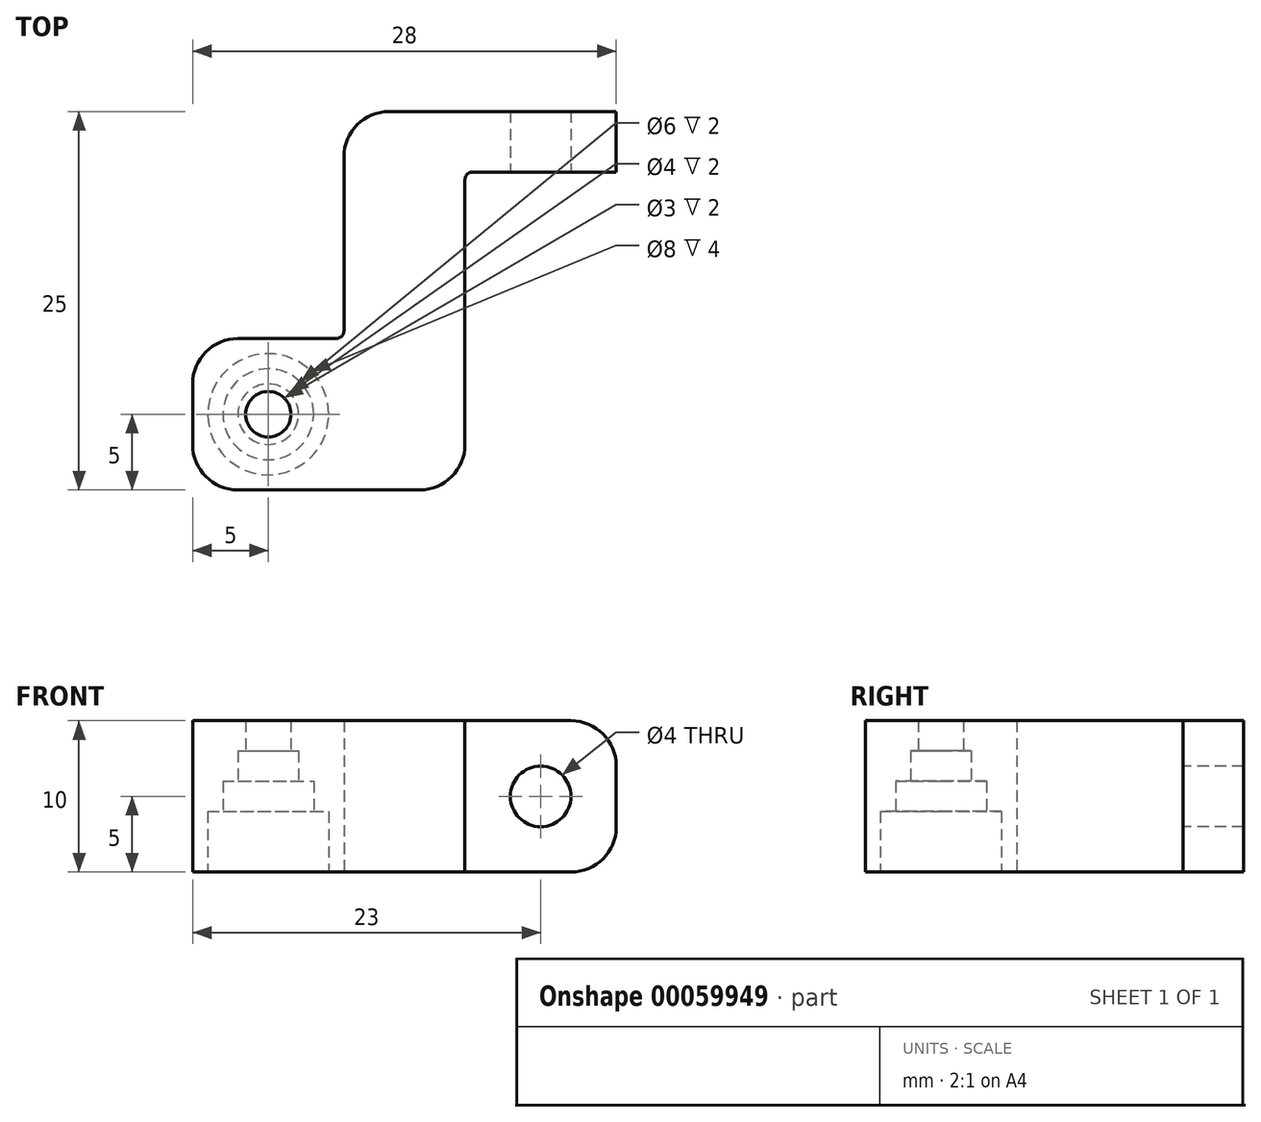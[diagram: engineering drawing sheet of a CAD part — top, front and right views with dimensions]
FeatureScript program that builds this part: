
annotation { "Feature Type Name" : "Feature", "Feature Type Description" : "" }
export const myFeature = defineFeature(function(context is Context, id is Id, definition is map)
    precondition{}
    {
        {
            var Q0;
            Q0=qCreatedBy(makeId("Top.planeOp"),FACE);
            var sketch = newSketch(context, id + "F0", { "sketchPlane" : qUnion([Q0])});
            skLineSegment(sketch, "E0.rect.bottom", {"start": v(4, 12.5) * mm, "end": v(-4, 12.5) * mm});
            skLineSegment(sketch, "E0.rect.top", {"start": v(4, -12.5) * mm, "end": v(-4, -12.5) * mm});
            skLineSegment(sketch, "E0.rect.left", {"start": v(4, 8.5) * mm, "end": v(4, -12.5) * mm});
            skLineSegment(sketch, "E0.rect.right", {"start": v(-4, 12.5) * mm, "end": v(-4, -2.5) * mm});
            skPoint(sketch, "E0.rect.middle", {"position": v(0, 0) * mm});
            skLineSegment(sketch, "E1.bottom", {"start": v(4, 12.5) * mm, "end": v(14, 12.5) * mm});
            skLineSegment(sketch, "E1.top", {"start": v(4, 8.5) * mm, "end": v(14, 8.5) * mm});
            skLineSegment(sketch, "E1.right", {"start": v(14, 12.5) * mm, "end": v(14, 8.5) * mm});
            skLineSegment(sketch, "E2.bottom", {"start": v(-4, -12.5) * mm, "end": v(-14, -12.5) * mm});
            skLineSegment(sketch, "E2.top", {"start": v(-4, -2.5) * mm, "end": v(-14, -2.5) * mm});
            skLineSegment(sketch, "E2.right", {"start": v(-14, -12.5) * mm, "end": v(-14, -2.5) * mm});
            skLineSegment(sketch, "E3", {"start": v(4, 8.5) * mm, "end": v(4, 12.5) * mm, "construction": true});
            skLineSegment(sketch, "E4", {"start": v(-4, -12.5) * mm, "end": v(-4, -2.5) * mm, "construction": true});
            skLineSegment(sketch, "E5", {"start": v(-4, -12.5) * mm, "end": v(-14, -2.5) * mm, "construction": true});
            skSolve(sketch);
        }
        {
            var Q0;
            Q0 = qSketchRegion(id + "F0", true);
            extrude(context, id + "F1", {"entities" : qUnion([Q0]), "depth" : 10 * mm});
        }
        {
            var Q0;
            Q0=makeQuery(id+"F1.opExtrude","SWEPT_EDGE",EDGE,{"disambiguationData":[OSD([sQuery(id+"F0.wireOp",EDGE,"E0.rect.bottom"),sQuery(id+"F0.wireOp",EDGE,"E0.rect.right")])]});
            var Q1;
            Q1=makeQuery(id+"F1.opExtrude","SWEPT_EDGE",EDGE,{"disambiguationData":[OSD([sQuery(id+"F0.wireOp",EDGE,"E0.rect.top"),sQuery(id+"F0.wireOp",EDGE,"E0.rect.left")])]});
            fillet(context, id + "F2", {"entities" : qUnion([Q0, Q1]), "radius" : 3 * mm, "tangentPropagation" : true, "allowEdgeOverflow" : false});
        }
        {
            var Q0;
            Q0=makeQuery(id+"F1.opExtrude","CAP_FACE",FACE,{"disambiguationData":[OSD([sQuery(id+"F0.wireOp",EDGE,"E0.rect.bottom"),sQuery(id+"F0.wireOp",EDGE,"E0.rect.top"),sQuery(id+"F0.wireOp",EDGE,"E0.rect.left"),sQuery(id+"F0.wireOp",EDGE,"E0.rect.right"),sQuery(id+"F0.wireOp",EDGE,"E1.bottom"),sQuery(id+"F0.wireOp",EDGE,"E1.top"),sQuery(id+"F0.wireOp",EDGE,"E1.right"),sQuery(id+"F0.wireOp",EDGE,"E2.bottom"),sQuery(id+"F0.wireOp",EDGE,"E2.top"),sQuery(id+"F0.wireOp",EDGE,"E2.right")])],"isStart":true});
            var sketch = newSketch(context, id + "F3", { "sketchPlane" : qUnion([Q0])});
            skLineSegment(sketch, "E6", {"start": v(-4, 2.5) * mm, "end": v(-14, 12.5) * mm, "construction": true});
            skCircle(sketch, "E7", {"center": v(-9, 7.5) * mm, "radius": 1.5 * mm});
            skSolve(sketch);
        }
        {
            var Q0;
            Q0 = qSketchRegion(id + "F3", true);
            extrude(context, id + "F4", {"entities" : qUnion([Q0]), "operationType" : NewBodyOperationType.REMOVE, "endBound" : BoundingType.THROUGH_ALL, "oppositeDirection" : true, "depth" : 25 * mm});
        }
        {
            var Q0;
            Q0=makeQuery(id+"F1.opExtrude","CAP_FACE",FACE,{"disambiguationData":[OSD([sQuery(id+"F0.wireOp",EDGE,"E0.rect.bottom"),sQuery(id+"F0.wireOp",EDGE,"E0.rect.top"),sQuery(id+"F0.wireOp",EDGE,"E0.rect.left"),sQuery(id+"F0.wireOp",EDGE,"E0.rect.right"),sQuery(id+"F0.wireOp",EDGE,"E1.bottom"),sQuery(id+"F0.wireOp",EDGE,"E1.top"),sQuery(id+"F0.wireOp",EDGE,"E1.right"),sQuery(id+"F0.wireOp",EDGE,"E2.bottom"),sQuery(id+"F0.wireOp",EDGE,"E2.top"),sQuery(id+"F0.wireOp",EDGE,"E2.right")])],"isStart":true});
            var sketch = newSketch(context, id + "F5", { "sketchPlane" : qUnion([Q0])});
            skCircle(sketch, "E8", {"center": v(-9, 7.5) * mm, "radius": 2 * mm});
            skSolve(sketch);
        }
        {
            var Q0;
            Q0 = qSketchRegion(id + "F5", true);
            extrude(context, id + "F6", {"entities" : qUnion([Q0]), "operationType" : NewBodyOperationType.REMOVE, "oppositeDirection" : true, "depth" : 8 * mm});
        }
        {
            var Q0;
            Q0=makeQuery(id+"F1.opExtrude","CAP_FACE",FACE,{"disambiguationData":[OSD([sQuery(id+"F0.wireOp",EDGE,"E0.rect.bottom"),sQuery(id+"F0.wireOp",EDGE,"E0.rect.top"),sQuery(id+"F0.wireOp",EDGE,"E0.rect.left"),sQuery(id+"F0.wireOp",EDGE,"E0.rect.right"),sQuery(id+"F0.wireOp",EDGE,"E1.bottom"),sQuery(id+"F0.wireOp",EDGE,"E1.top"),sQuery(id+"F0.wireOp",EDGE,"E1.right"),sQuery(id+"F0.wireOp",EDGE,"E2.bottom"),sQuery(id+"F0.wireOp",EDGE,"E2.top"),sQuery(id+"F0.wireOp",EDGE,"E2.right")])],"isStart":true});
            var sketch = newSketch(context, id + "F7", { "sketchPlane" : qUnion([Q0])});
            skCircle(sketch, "E9", {"center": v(-9, 7.5) * mm, "radius": 3 * mm});
            skSolve(sketch);
        }
        {
            var Q0;
            Q0 = qSketchRegion(id + "F7", true);
            extrude(context, id + "F8", {"entities" : qUnion([Q0]), "operationType" : NewBodyOperationType.REMOVE, "oppositeDirection" : true, "depth" : 6 * mm});
        }
        {
            var Q0;
            Q0=makeQuery(id+"F1.opExtrude","CAP_FACE",FACE,{"disambiguationData":[OSD([sQuery(id+"F0.wireOp",EDGE,"E0.rect.bottom"),sQuery(id+"F0.wireOp",EDGE,"E0.rect.top"),sQuery(id+"F0.wireOp",EDGE,"E0.rect.left"),sQuery(id+"F0.wireOp",EDGE,"E0.rect.right"),sQuery(id+"F0.wireOp",EDGE,"E1.bottom"),sQuery(id+"F0.wireOp",EDGE,"E1.top"),sQuery(id+"F0.wireOp",EDGE,"E1.right"),sQuery(id+"F0.wireOp",EDGE,"E2.bottom"),sQuery(id+"F0.wireOp",EDGE,"E2.top"),sQuery(id+"F0.wireOp",EDGE,"E2.right")])],"isStart":true});
            var sketch = newSketch(context, id + "F9", { "sketchPlane" : qUnion([Q0])});
            skCircle(sketch, "E10", {"center": v(-9, 7.5) * mm, "radius": 4 * mm});
            skSolve(sketch);
        }
        {
            var Q0;
            Q0 = qSketchRegion(id + "F9", true);
            extrude(context, id + "F10", {"entities" : qUnion([Q0]), "operationType" : NewBodyOperationType.REMOVE, "oppositeDirection" : true, "depth" : 4 * mm});
        }
        {
            var Q0;
            Q0=makeQuery(id+"F1.opExtrude","SWEPT_EDGE",EDGE,{"disambiguationData":[OSD([sQuery(id+"F0.wireOp",EDGE,"E2.top"),sQuery(id+"F0.wireOp",EDGE,"E2.right")])]});
            var Q1;
            Q1=makeQuery(id+"F1.opExtrude","SWEPT_EDGE",EDGE,{"disambiguationData":[OSD([sQuery(id+"F0.wireOp",EDGE,"E2.bottom"),sQuery(id+"F0.wireOp",EDGE,"E2.right")])]});
            fillet(context, id + "F11", {"entities" : qUnion([Q0, Q1]), "radius" : 3 * mm, "tangentPropagation" : true, "allowEdgeOverflow" : false});
        }
        {
            var Q0;
            Q0=makeQuery(id+"F1.opExtrude","SWEPT_FACE",FACE,{"disambiguationData":[OSD([sQuery(id+"F0.wireOp",EDGE,"E1.top")])]});
            var sketch = newSketch(context, id + "F12", { "sketchPlane" : qUnion([Q0])});
            skLineSegment(sketch, "E11", {"start": v(4, 0) * mm, "end": v(14, 10) * mm, "construction": true});
            skCircle(sketch, "E12", {"center": v(9, 5) * mm, "radius": 2 * mm});
            skSolve(sketch);
        }
        {
            var Q0;
            Q0 = qSketchRegion(id + "F12", true);
            extrude(context, id + "F13", {"entities" : qUnion([Q0]), "operationType" : NewBodyOperationType.REMOVE, "endBound" : BoundingType.THROUGH_ALL, "oppositeDirection" : true, "depth" : 25 * mm});
        }
        {
            var Q0;
            Q0=makeQuery(id+"F1.opExtrude","CAP_EDGE",EDGE,{"disambiguationData":[OSD([sQuery(id+"F0.wireOp",EDGE,"E1.right")])],"isStart":true});
            var Q1;
            Q1=makeQuery(id+"F1.opExtrude","CAP_EDGE",EDGE,{"disambiguationData":[OSD([sQuery(id+"F0.wireOp",EDGE,"E1.right")])],"isStart":false});
            fillet(context, id + "F14", {"entities" : qUnion([Q0, Q1]), "radius" : 3 * mm, "tangentPropagation" : true, "allowEdgeOverflow" : false});
        }
        {
            var Q0;
            Q0=makeQuery(id+"F1.opExtrude","SWEPT_EDGE",EDGE,{"disambiguationData":[OSD([sQuery(id+"F0.wireOp",EDGE,"E0.rect.left"),sQuery(id+"F0.wireOp",EDGE,"E1.top")])]});
            var Q1;
            Q1=makeQuery(id+"F1.opExtrude","SWEPT_EDGE",EDGE,{"disambiguationData":[OSD([sQuery(id+"F0.wireOp",EDGE,"E0.rect.right"),sQuery(id+"F0.wireOp",EDGE,"E2.top")])]});
            fillet(context, id + "F15", {"entities" : qUnion([Q0, Q1]), "radius" : 0.5 * mm, "tangentPropagation" : true, "allowEdgeOverflow" : false});
        }
    });
